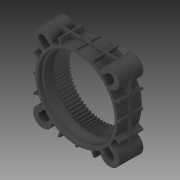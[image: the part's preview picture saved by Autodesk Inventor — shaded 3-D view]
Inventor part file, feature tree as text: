
AUTODESK INVENTOR PART (.ipt)
format: ipt  version: 2019 (Build 230136000, 136)  size: 1,931,776 bytes
history: native  units: in
note: dims shown in document units (in); Inventor stores cm internally (conversion verified against a paired STEP export)
features: fillet x1
ambient origin geometry x8: Origin, YZ Plane, XZ Plane, XY Plane, X Axis, Y Axis, Z Axis, Center Point
bodies: Solid1 (feature_tree)
feature tree (1):
  fillet  "Fillet12"  [1 undecoded]
note: 1 required parameter value undecoded (feature->parameter linkage not recoverable at this tier; creation-order binding heuristic only, values carry confidence <= 0.55)
